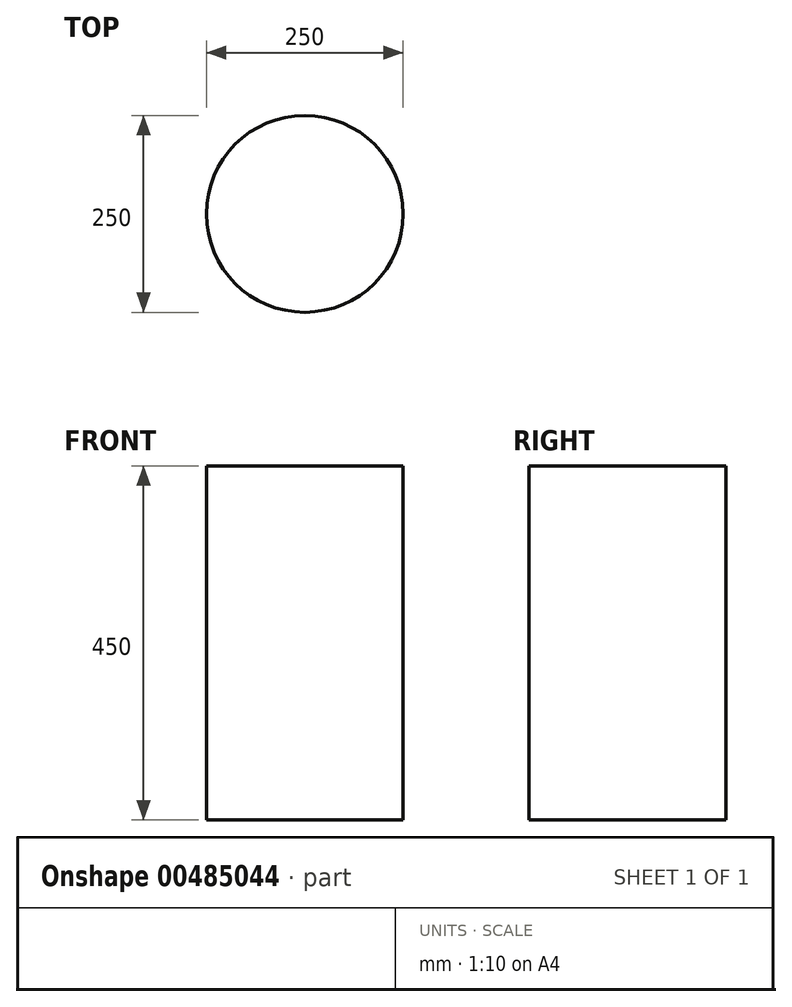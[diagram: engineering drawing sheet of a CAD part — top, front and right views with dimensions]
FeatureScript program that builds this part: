
annotation { "Feature Type Name" : "Feature", "Feature Type Description" : "" }
export const myFeature = defineFeature(function(context is Context, id is Id, definition is map)
    precondition{}
    {
        {
            var Q0;
            Q0=qCreatedBy(makeId("Top.planeOp"),FACE);
            var sketch = newSketch(context, id + "F0", { "sketchPlane" : qUnion([Q0])});
            skCircle(sketch, "E0", {"center": v(0, 0) * mm, "radius": 125 * mm});
            skSolve(sketch);
        }
        {
            var Q0;
            Q0 = qSketchRegion(id + "F0", true);
            extrude(context, id + "F1", {"entities" : qUnion([Q0]), "depth" : 450 * mm});
        }
    });
